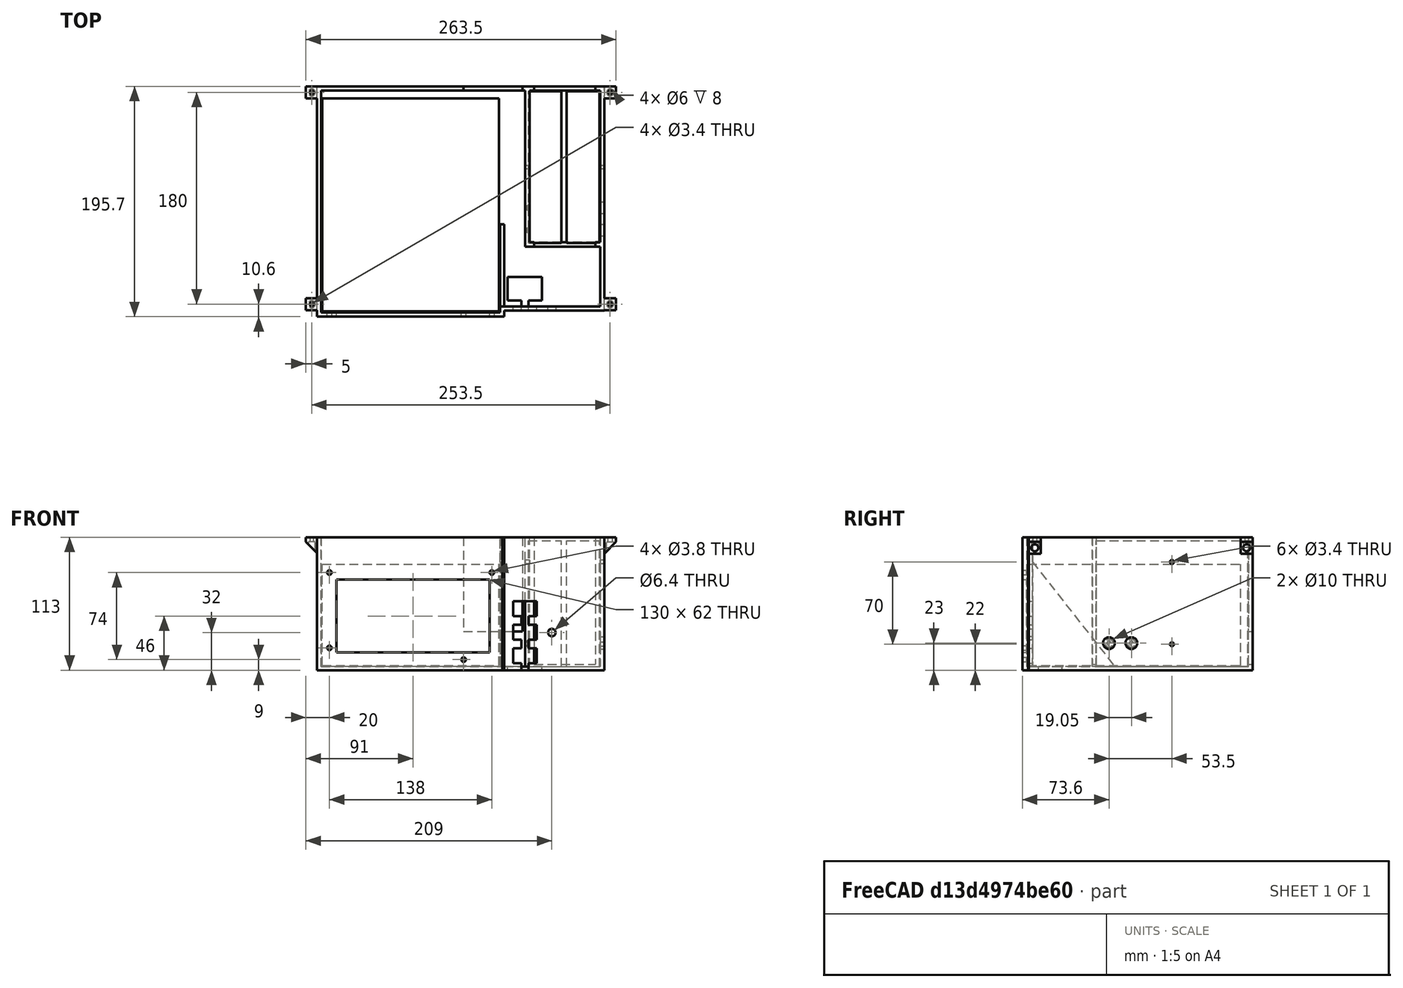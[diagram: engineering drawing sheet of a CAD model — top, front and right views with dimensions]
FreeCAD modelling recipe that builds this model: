
FCSTD DOCUMENT  (FreeCAD 0.20R2887)
Label: HiCoHolderPt3-Thicc
License: All rights reserved
LicenseURL: http://en.wikipedia.org/wiki/All_rights_reserved
objects: Part::Box×32, Part::Cylinder×19, Part::MultiFuse×18, Part::Cut×11, Part::Wedge×5, Part::Cone×2
note: 87 computed .brp shape members not serialized (recipe doc carries the construction recipe); baked Part::Feature solids carry a one-line shape summary decoded from their .brp

FEATURE [Part::Box] Box  label="PSUPanelPlate"
  AttacherType = Attacher::AttachEngine3D
  Height = 113
  Length = 156
  Placement = pos=(-3,-3.6,-3) rot=(0,0,1;0rad)
  Width = 3.6
FEATURE [Part::Box] Box001  label="PSUblob"
  AttacherType = Attacher::AttachEngine3D
  Height = 86
  Length = 150
  Placement = pos=(0,-4,1) rot=(0,0,1;0rad)
  Width = 181
FEATURE [Part::Box] Box002  label="Cube001"
  AttacherType = Attacher::AttachEngine3D
  Height = 62
  Length = 130
  Placement = pos=(12,-3.6,12) rot=(0,0,1;0rad)
  Width = 3.6
FEATURE [Part::Cylinder] Cylinder
  Angle = 360
  AttacherType = Attacher::AttachEngine3D
  FirstAngle = 0
  Height = 10
  Placement = pos=(6,0,16) rot=(1,0,0;1.5708rad)
  Radius = 1.9
  SecondAngle = 0
FEATURE [Part::Cylinder] Cylinder001
  Angle = 360
  AttacherType = Attacher::AttachEngine3D
  FirstAngle = 0
  Height = 10
  Placement = pos=(6,0,80) rot=(1,0,0;1.5708rad)
  Radius = 1.9
  SecondAngle = 0
FEATURE [Part::Cylinder] Cylinder002
  Angle = 360
  AttacherType = Attacher::AttachEngine3D
  FirstAngle = 0
  Height = 10
  Placement = pos=(144,0,80) rot=(1,0,0;1.5708rad)
  Radius = 1.9
  SecondAngle = 0
FEATURE [Part::Cylinder] Cylinder003
  Angle = 360
  AttacherType = Attacher::AttachEngine3D
  FirstAngle = 0
  Height = 10
  Placement = pos=(120,0,6) rot=(1,0,0;1.5708rad)
  Radius = 1.9
  SecondAngle = 0
FEATURE [Part::MultiFuse] Fusion  label="PSU PanelHoles"
  Shapes = -> [Cylinder,Cylinder001,Cylinder002,Cylinder003,Box002]
FEATURE [Part::Cut] Cut  label="PSUPanel"
  Base = -> Box
  Placement = pos=(0,-5,0) rot=(0,0,1;0rad)
  Tool = -> Fusion
FEATURE [Part::Box] Box003  label="BasePlate"
  AttacherType = Attacher::AttachEngine3D
  Height = 3
  Length = 244.2
  Placement = pos=(-4.6,-0.1,-3) rot=(0,0,1;0rad)
  Width = 186.2
FEATURE [Part::Cylinder] Cylinder004  label="PowerConnectorScrew2"
  Angle = 360
  AttacherType = Attacher::AttachEngine3D
  FirstAngle = 0
  Height = 10
  Radius = 1.7
  SecondAngle = 0
FEATURE [Part::Cylinder] Cylinder005  label="PowerConnectorScrew1"
  Angle = 360
  AttacherType = Attacher::AttachEngine3D
  FirstAngle = 0
  Height = 10
  Placement = pos=(0,19.05,0) rot=(0,0,1;0rad)
  Radius = 1.7
  SecondAngle = 0
FEATURE [Part::Wedge] Wedge001  label="RightPSUPanelSupport"
  AttacherType = Attacher::AttachEngine3D
  Placement = pos=(151,0,0) rot=(0,0,1;0rad)
  X2max = 3.6
  X2min = 0
  Xmax = 3.6
  Xmin = 0
  Ymax = 70
  Ymin = 0
  Z2max = 0
  Z2min = -3
  Zmax = 89
  Zmin = -3
FEATURE [Part::Box] Box004  label="SwitchPanel"
  AttacherType = Attacher::AttachEngine3D
  Height = 113
  Length = 86.5
  Placement = pos=(153,-3.6,-3) rot=(0,0,1;0rad)
  Width = 3.6
FEATURE [Part::Box] Box006  label="Cube003"
  AttacherType = Attacher::AttachEngine3D
  Height = 19.2
  Length = 6
  Placement = pos=(164,-5,-6) rot=(0,0,1;0rad)
  Width = 7
FEATURE [Part::Box] Box007  label="Cube004"
  AttacherType = Attacher::AttachEngine3D
  Height = 12.7
  Length = 20
  Placement = pos=(157,-5,3) rot=(0,0,1;0rad)
  Width = 7
FEATURE [Part::Box] Box008  label="Cube005"
  AttacherType = Attacher::AttachEngine3D
  Height = 19.2
  Length = 6
  Placement = pos=(164,-5,-6) rot=(0,0,1;0rad)
  Width = 7
FEATURE [Part::MultiFuse] Fusion003  label="ButtonCutout001"
  Placement = pos=(5,0,20) rot=(0,0,1;0rad)
  Shapes = -> [Box007,Box008]
FEATURE [Part::Box] Box009  label="Cube006"
  AttacherType = Attacher::AttachEngine3D
  Height = 12.7
  Length = 20
  Placement = pos=(157,-5,3) rot=(0,0,1;0rad)
  Width = 7
FEATURE [Part::Box] Box010  label="Cube007"
  AttacherType = Attacher::AttachEngine3D
  Height = 19.2
  Length = 6
  Placement = pos=(164,-5,-6) rot=(0,0,1;0rad)
  Width = 7
FEATURE [Part::MultiFuse] Fusion004  label="ButtonCutout002"
  Placement = pos=(5,0,40) rot=(0,0,1;0rad)
  Shapes = -> [Box009,Box010]
FEATURE [Part::Cylinder] Cylinder006
  Angle = 360
  AttacherType = Attacher::AttachEngine3D
  FirstAngle = 0
  Height = 10
  Placement = pos=(195,0,29) rot=(1,0,0;1.5708rad)
  Radius = 3.2
  SecondAngle = 0
FEATURE [Part::Box] Box011  label="NetLionblob"
  AttacherType = Attacher::AttachEngine3D
  Height = 107
  Length = 28
  Placement = pos=(207.5,54,0) rot=(0,0,1;0rad)
  Width = 129
FEATURE [Part::Box] Box012  label="NetLionblob001"
  AttacherType = Attacher::AttachEngine3D
  Height = 107
  Length = 28
  Placement = pos=(175,54,0) rot=(0,0,1;0rad)
  Width = 129
FEATURE [Part::Box] Box013  label="OuterBox"
  AttacherType = Attacher::AttachEngine3D
  Height = 113
  Length = 67.2
  Placement = pos=(179.4,50.9,-3) rot=(0,0,1;0rad)
  Width = 136.2
FEATURE [Part::Box] Box014  label="Cube008"
  AttacherType = Attacher::AttachEngine3D
  Height = 113
  Length = 60
  Placement = pos=(183,54.5,0) rot=(0,0,1;0rad)
  Width = 129
FEATURE [Part::Box] Box015  label="Cube009"
  AttacherType = Attacher::AttachEngine3D
  Height = 113
  Length = 52
  Placement = pos=(187,48,2) rot=(0,0,1;0rad)
  Width = 142
FEATURE [Part::MultiFuse] Fusion006  label="NetLionCutouts"
  Shapes = -> [Box015,Box014]
FEATURE [Part::Cut] Cut003  label="SlicedBox"
  Base = -> Box013
  Tool = -> Fusion006
FEATURE [Part::Cone] Cone  label="PowerConnectorScrewCountersink1"
  Angle = 360
  AttacherType = Attacher::AttachEngine3D
  Height = 3.8278
  Radius1 = 3.3264
  Radius2 = 0
FEATURE [Part::Cone] Cone001  label="PowerConnectorScrewCountersink2"
  Angle = 360
  AttacherType = Attacher::AttachEngine3D
  Height = 3.83
  Placement = pos=(0,19.05,0) rot=(0,0,1;0rad)
  Radius1 = 3.33
  Radius2 = 0
FEATURE [Part::Cylinder] Cylinder007  label="ScrewdriverAccess2"
  Angle = 360
  AttacherType = Attacher::AttachEngine3D
  FirstAngle = 0
  Height = 10
  Placement = pos=(0,0,-66) rot=(0,0,1;0rad)
  Radius = 5
  SecondAngle = 0
FEATURE [Part::Cylinder] Cylinder008  label="ScrewdriverAccess1"
  Angle = 360
  AttacherType = Attacher::AttachEngine3D
  FirstAngle = 0
  Height = 10
  Placement = pos=(0,19.05,-66) rot=(0,0,1;0rad)
  Radius = 5
  SecondAngle = 0
FEATURE [Part::MultiFuse] Fusion001  label="PowerConnectorHoles"
  Placement = pos=(183,65,20) rot=(0,1,0;-1.5708rad)
  Shapes = -> [Cylinder005,Cylinder004,Cone,Cone001,Cylinder008,Cylinder007]
FEATURE [Part::Cut] Cut004  label="BoxWithPowerConnector"
  Base = -> Cut003
  Tool = -> Fusion001
FEATURE [Part::Cylinder] Cylinder009
  Angle = 360
  AttacherType = Attacher::AttachEngine3D
  FirstAngle = 0
  Height = 100
  Placement = pos=(0,0,0) rot=(0,1,0;1.5708rad)
  Radius = 1.7
  SecondAngle = 0
FEATURE [Part::Cylinder] Cylinder010
  Angle = 360
  AttacherType = Attacher::AttachEngine3D
  FirstAngle = 0
  Height = 100
  Placement = pos=(0,70,0) rot=(0,1,0;1.5708rad)
  Radius = 1.7
  SecondAngle = 0
FEATURE [Part::MultiFuse] Fusion007  label="NetLionMountHoles"
  Placement = pos=(179,118.5,19) rot=(1,0,0;1.5708rad)
  Shapes = -> [Cylinder010,Cylinder009]
FEATURE [Part::Cut] Cut005  label="NetLionMountBox"
  Base = -> Cut004
  Placement = pos=(-7,0,0) rot=(0,0,1;0rad)
  Tool = -> Fusion007
FEATURE [Part::Box] Box016  label="Cube"
  AttacherType = Attacher::AttachEngine3D
  Height = 110
  Length = 3
  Placement = pos=(-4,-3,0) rot=(0,0,1;0rad)
  Width = 10
FEATURE [Part::Box] Box017  label="Cube010"
  AttacherType = Attacher::AttachEngine3D
  Height = 4
  Length = 13
  Placement = pos=(-14,-3,106) rot=(0,0,1;0rad)
  Width = 10
FEATURE [Part::Cylinder] Cylinder011
  Angle = 360
  AttacherType = Attacher::AttachEngine3D
  FirstAngle = 0
  Height = 40
  Placement = pos=(-9,2,70) rot=(0,0,1;0rad)
  Radius = 1.7
  SecondAngle = 0
FEATURE [Part::Cylinder] Cylinder012
  Angle = 360
  AttacherType = Attacher::AttachEngine3D
  FirstAngle = 0
  Height = 36
  Placement = pos=(-9,2,70) rot=(0,0,1;0rad)
  Radius = 3
  SecondAngle = 0
FEATURE [Part::Wedge] Wedge002  label="Wedge"
  AttacherType = Attacher::AttachEngine3D
  Placement = pos=(-4,-3,96) rot=(0,0,1;1.5708rad)
  X2max = 10
  X2min = 0
  Xmax = 10
  Xmin = 0
  Ymax = 10
  Ymin = 0
  Z2max = 10
  Z2min = 10
  Zmax = 10
  Zmin = 0
FEATURE [Part::MultiFuse] Fusion008  label="SupportArm"
  Shapes = -> [Box016,Box017,Wedge002]
FEATURE [Part::MultiFuse] Fusion009  label="CounterboredHole"
  Shapes = -> [Cylinder012,Cylinder011]
FEATURE [Part::Cut] Cut006  label="Mount"
  Base = -> Fusion008
  Tool = -> Fusion009
FEATURE [Part::Box] Box018  label="Cube011"
  AttacherType = Attacher::AttachEngine3D
  Height = 4
  Length = 13
  Placement = pos=(-14,-3,106) rot=(0,0,1;0rad)
  Width = 10
FEATURE [Part::Cylinder] Cylinder013
  Angle = 360
  AttacherType = Attacher::AttachEngine3D
  FirstAngle = 0
  Height = 40
  Placement = pos=(-9,2,70) rot=(0,0,1;0rad)
  Radius = 1.7
  SecondAngle = 0
FEATURE [Part::Cylinder] Cylinder014
  Angle = 360
  AttacherType = Attacher::AttachEngine3D
  FirstAngle = 0
  Height = 36
  Placement = pos=(-9,2,70) rot=(0,0,1;0rad)
  Radius = 3
  SecondAngle = 0
FEATURE [Part::MultiFuse] Fusion011  label="CounterboredHole001"
  Shapes = -> [Cylinder014,Cylinder013]
FEATURE [Part::Wedge] Wedge003
  AttacherType = Attacher::AttachEngine3D
  Placement = pos=(-4,-3,96) rot=(0,0,1;1.5708rad)
  X2max = 10
  X2min = 0
  Xmax = 10
  Xmin = 0
  Ymax = 10
  Ymin = 0
  Z2max = 10
  Z2min = 10
  Zmax = 10
  Zmin = 0
FEATURE [Part::Box] Box019  label="Cube012"
  AttacherType = Attacher::AttachEngine3D
  Height = 110
  Length = 3
  Placement = pos=(-4,-3,0) rot=(0,0,1;0rad)
  Width = 10
FEATURE [Part::MultiFuse] Fusion010  label="SupportArm001"
  Shapes = -> [Box019,Box018,Wedge003]
FEATURE [Part::Cut] Cut007  label="Mount001"
  Base = -> Fusion010
  Placement = pos=(0,180,0) rot=(0,0,1;0rad)
  Tool = -> Fusion011
FEATURE [Part::Box] Box020  label="Cube013"
  AttacherType = Attacher::AttachEngine3D
  Height = 4
  Length = 13.5
  Placement = pos=(-14,-3,106) rot=(0,0,1;0rad)
  Width = 10
FEATURE [Part::Cylinder] Cylinder015
  Angle = 360
  AttacherType = Attacher::AttachEngine3D
  FirstAngle = 0
  Height = 40
  Placement = pos=(-9,2,70) rot=(0,0,1;0rad)
  Radius = 1.7
  SecondAngle = 0
FEATURE [Part::Cylinder] Cylinder016
  Angle = 360
  AttacherType = Attacher::AttachEngine3D
  FirstAngle = 0
  Height = 36
  Placement = pos=(-9,2,70) rot=(0,0,1;0rad)
  Radius = 3
  SecondAngle = 0
FEATURE [Part::MultiFuse] Fusion013  label="CounterboredHole002"
  Shapes = -> [Cylinder016,Cylinder015]
FEATURE [Part::Wedge] Wedge004
  AttacherType = Attacher::AttachEngine3D
  Placement = pos=(-4,-3,96) rot=(0,0,1;1.5708rad)
  X2max = 10
  X2min = 0
  Xmax = 10
  Xmin = 0
  Ymax = 10
  Ymin = 0
  Z2max = 10
  Z2min = 10
  Zmax = 10
  Zmin = 0
FEATURE [Part::Box] Box021  label="Cube014"
  AttacherType = Attacher::AttachEngine3D
  Height = 110
  Length = 3.5
  Placement = pos=(-4,-3,0) rot=(0,0,1;0rad)
  Width = 10
FEATURE [Part::MultiFuse] Fusion012  label="SupportArm002"
  Shapes = -> [Box021,Box020,Wedge004]
FEATURE [Part::Cut] Cut008  label="Mount002"
  Base = -> Fusion012
  Placement = pos=(235.5,4,0) rot=(0,0,1;3.14159rad)
  Tool = -> Fusion013
FEATURE [Part::Cylinder] Cylinder017
  Angle = 360
  AttacherType = Attacher::AttachEngine3D
  FirstAngle = 0
  Height = 36
  Placement = pos=(-9,2,70) rot=(0,0,1;0rad)
  Radius = 3
  SecondAngle = 0
FEATURE [Part::Box] Box022  label="Cube015"
  AttacherType = Attacher::AttachEngine3D
  Height = 110
  Length = 3.5
  Placement = pos=(-4,-3,0) rot=(0,0,1;0rad)
  Width = 10
FEATURE [Part::Wedge] Wedge005
  AttacherType = Attacher::AttachEngine3D
  Placement = pos=(-4,-3,96) rot=(0,0,1;1.5708rad)
  X2max = 10
  X2min = 0
  Xmax = 10
  Xmin = 0
  Ymax = 10
  Ymin = 0
  Z2max = 10
  Z2min = 10
  Zmax = 10
  Zmin = 0
FEATURE [Part::Cylinder] Cylinder018
  Angle = 360
  AttacherType = Attacher::AttachEngine3D
  FirstAngle = 0
  Height = 40
  Placement = pos=(-9,2,70) rot=(0,0,1;0rad)
  Radius = 1.7
  SecondAngle = 0
FEATURE [Part::MultiFuse] Fusion015  label="CounterboredHole003"
  Shapes = -> [Cylinder017,Cylinder018]
FEATURE [Part::Box] Box023  label="Cube016"
  AttacherType = Attacher::AttachEngine3D
  Height = 4
  Length = 13.5
  Placement = pos=(-14,-3,106) rot=(0,0,1;0rad)
  Width = 10
FEATURE [Part::MultiFuse] Fusion014  label="SupportArm003"
  Shapes = -> [Box022,Box023,Wedge005]
FEATURE [Part::Cut] Cut009  label="Mount003"
  Base = -> Fusion014
  Placement = pos=(235.5,184,0) rot=(0,0,1;3.14159rad)
  Tool = -> Fusion015
FEATURE [Part::Box] Box024  label="Cube017"
  AttacherType = Attacher::AttachEngine3D
  Height = 19.2
  Length = 6
  Placement = pos=(169,-3,-3) rot=(0,0,1;0rad)
  Width = 20
FEATURE [Part::Box] Box027  label="Cube020"
  AttacherType = Attacher::AttachEngine3D
  Height = 19.2
  Length = 29
  Placement = pos=(157.5,5,-3) rot=(0,0,1;0rad)
  Width = 20
FEATURE [Part::MultiFuse] Fusion016  label="SwitchAccessCuts"
  Shapes = -> [Box024,Box027]
FEATURE [Part::Cut] Cut010  label="Bottom"
  Base = -> Box003
  Tool = -> Fusion016
FEATURE [Part::Box] Box028  label="LeftSide"
  AttacherType = Attacher::AttachEngine3D
  Height = 113
  Length = 3.6
  Placement = pos=(-4.6,-8.6,-3) rot=(0,0,1;0rad)
  Width = 195.7
FEATURE [Part::Box] Box029  label="RightSide"
  AttacherType = Attacher::AttachEngine3D
  Height = 113
  Length = 3.6
  Placement = pos=(236,-3,-3) rot=(0,0,1;0rad)
  Width = 60
FEATURE [Part::Box] Box030  label="Back"
  AttacherType = Attacher::AttachEngine3D
  Height = 113
  Length = 180.5
  Placement = pos=(-3,183.5,-3) rot=(0,0,1;0rad)
  Width = 3.6
FEATURE [Part::Box] Box031  label="CordCutout"
  AttacherType = Attacher::AttachEngine3D
  Height = 80
  Length = 50
  Placement = pos=(120,180,30) rot=(0,0,1;0rad)
  Width = 10
FEATURE [Part::Box] Box032  label="PSURightFill"
  AttacherType = Attacher::AttachEngine3D
  Height = 113
  Length = 3.6
  Placement = pos=(151,-8.5,-3) rot=(0,0,1;0rad)
  Width = 8.5
FEATURE [Part::Box] Box033  label="PSUBottomFill"
  AttacherType = Attacher::AttachEngine3D
  Height = 3
  Length = 158
  Placement = pos=(-4.6,-8.5,-3) rot=(0,0,1;0rad)
  Width = 8.5
FEATURE [Part::Box] Box005  label="Cube002"
  AttacherType = Attacher::AttachEngine3D
  Height = 12.7
  Length = 20
  Placement = pos=(157,-5,3) rot=(0,0,1;0rad)
  Width = 7
FEATURE [Part::MultiFuse] Fusion002  label="ButtonCutout"
  Placement = pos=(5,0,0) rot=(0,0,1;0rad)
  Shapes = -> [Box005,Box006]
FEATURE [Part::MultiFuse] Fusion005  label="SwitchHoles"
  Shapes = -> [Cylinder006,Fusion002,Fusion003,Fusion004]
FEATURE [Part::Cut] Cut002  label="SwitchMounts"
  Base = -> Box004
  Tool = -> Fusion005
FEATURE [Part::MultiFuse] Fusion017  label="HiCoAuxBox"
  Shapes = -> [Cut,Wedge001,Cut002,Cut005,Cut006,Cut007,Cut008,Cut009,Cut010,Box028,Box029,Box030,Box032,Box033]
FEATURE [Part::Cut] Cut011  label="HiCoAux"
  Base = -> Fusion017
  Tool = -> Box031
